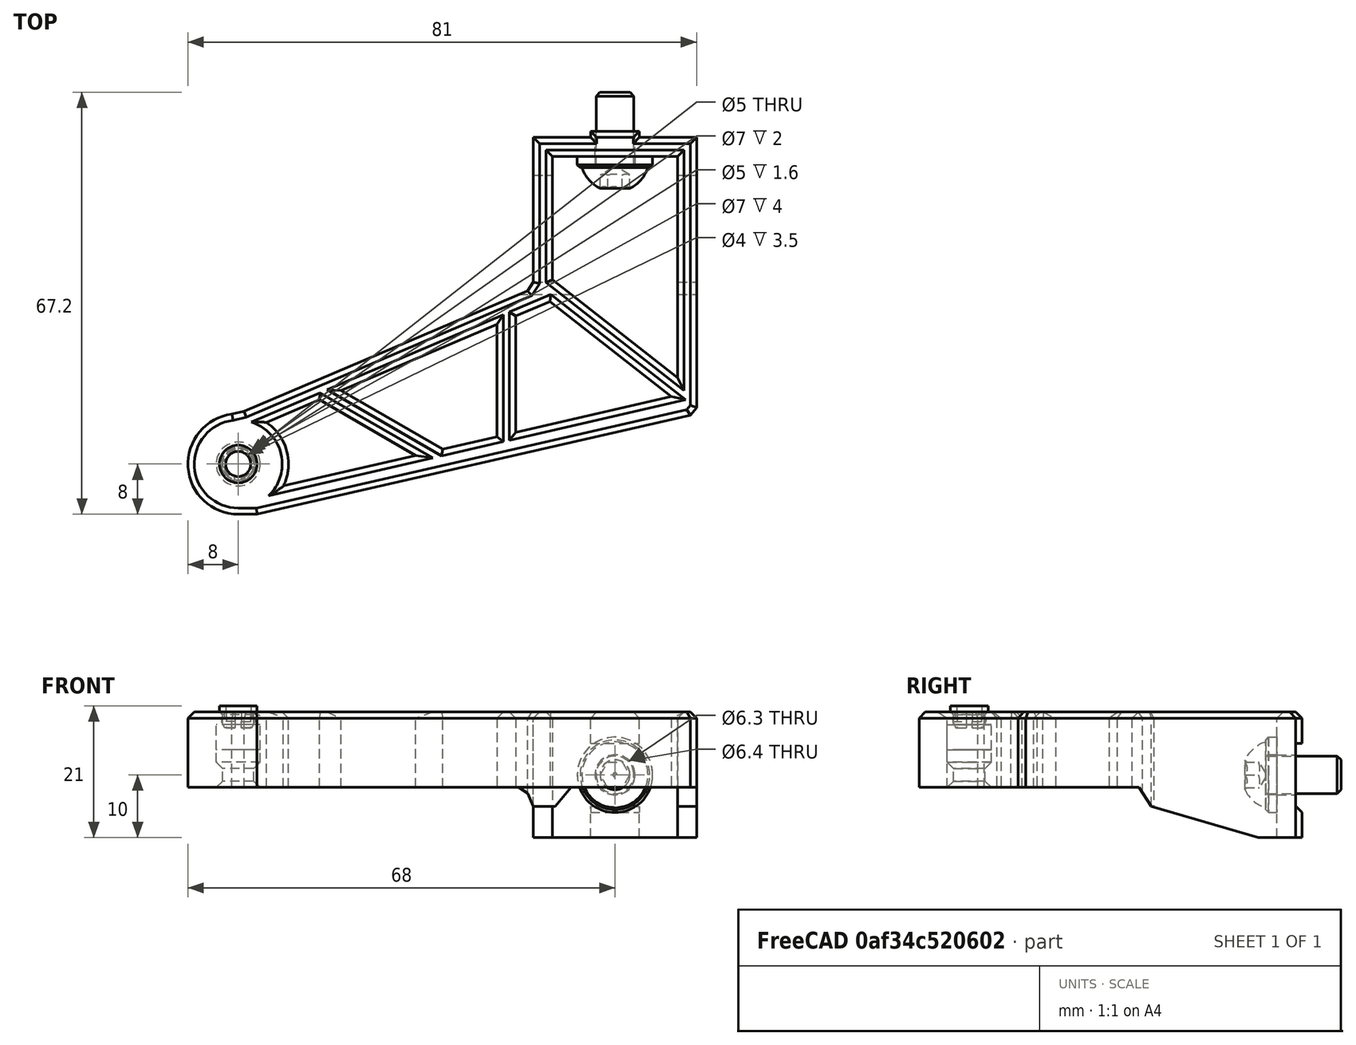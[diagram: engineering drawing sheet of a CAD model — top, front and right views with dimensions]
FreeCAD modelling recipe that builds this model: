
FCSTD DOCUMENT  (FreeCAD 0.19R24291 (Git))
Label: addon-filament-guide-arm-assembly
License: All rights reserved
LicenseURL: http://en.wikipedia.org/wiki/All_rights_reserved
objects: Part::FeaturePython×2, Part::Feature×2, PartDesign::CoordinateSystem×1, App::Part×1
note: 5 computed .brp shape members not serialized (recipe doc carries the construction recipe); baked Part::Feature solids carry a one-line shape summary decoded from their .brp

FEATURE [Part::FeaturePython] Screw009  label="M6x12-Screw"  # Fasteners workbench fastener (typed FeaturePython)
  Placement = pos=(0,-4.8,10) rot=(1,0,0;1.5708rad)
  baseObject = -> Washer [Edge1]
  diameter = 4
  invert = false
  length = 1
  lengthCustom = 12
  matchOuter = true
  offset = 0
  thread = false
  type = 40
FEATURE [Part::FeaturePython] Washer  label="M6-Washer"  # Fasteners workbench fastener (typed FeaturePython)
  Placement = pos=(0,-3,10) rot=(1,0,0;1.5708rad)
  diameter = 2
  invert = true
  matchOuter = true
  offset = 0
  type = 4
FEATURE [PartDesign::CoordinateSystem] LCS_filament_guide  label="LCS_filament-guide"
  AttacherType = Attacher::AttachEngine3D
FEATURE [Part::Feature] Chamfer001002001001  label="filament-guide-e3d-collet"
  Placement = pos=(0,-2,0) rot=(0,1,0;3.14159rad)
  shape: bbox 81 x 61 x 20 mm, 85 faces (baked)
FEATURE [Part::Feature] Cut001001001  label="E3D-bowden-collet"
  Placement = pos=(-60,-52,21) rot=(0,1,0;3.14159rad)
  shape: bbox 6 x 6 x 3.5 mm, 32 faces (baked)
FEATURE [App::Part] Part002  label="filament-guide"
  Group = -> [Washer,Screw009,LCS_filament_guide,Chamfer001002001001,Cut001001001]
  Origin = -> Origin002
